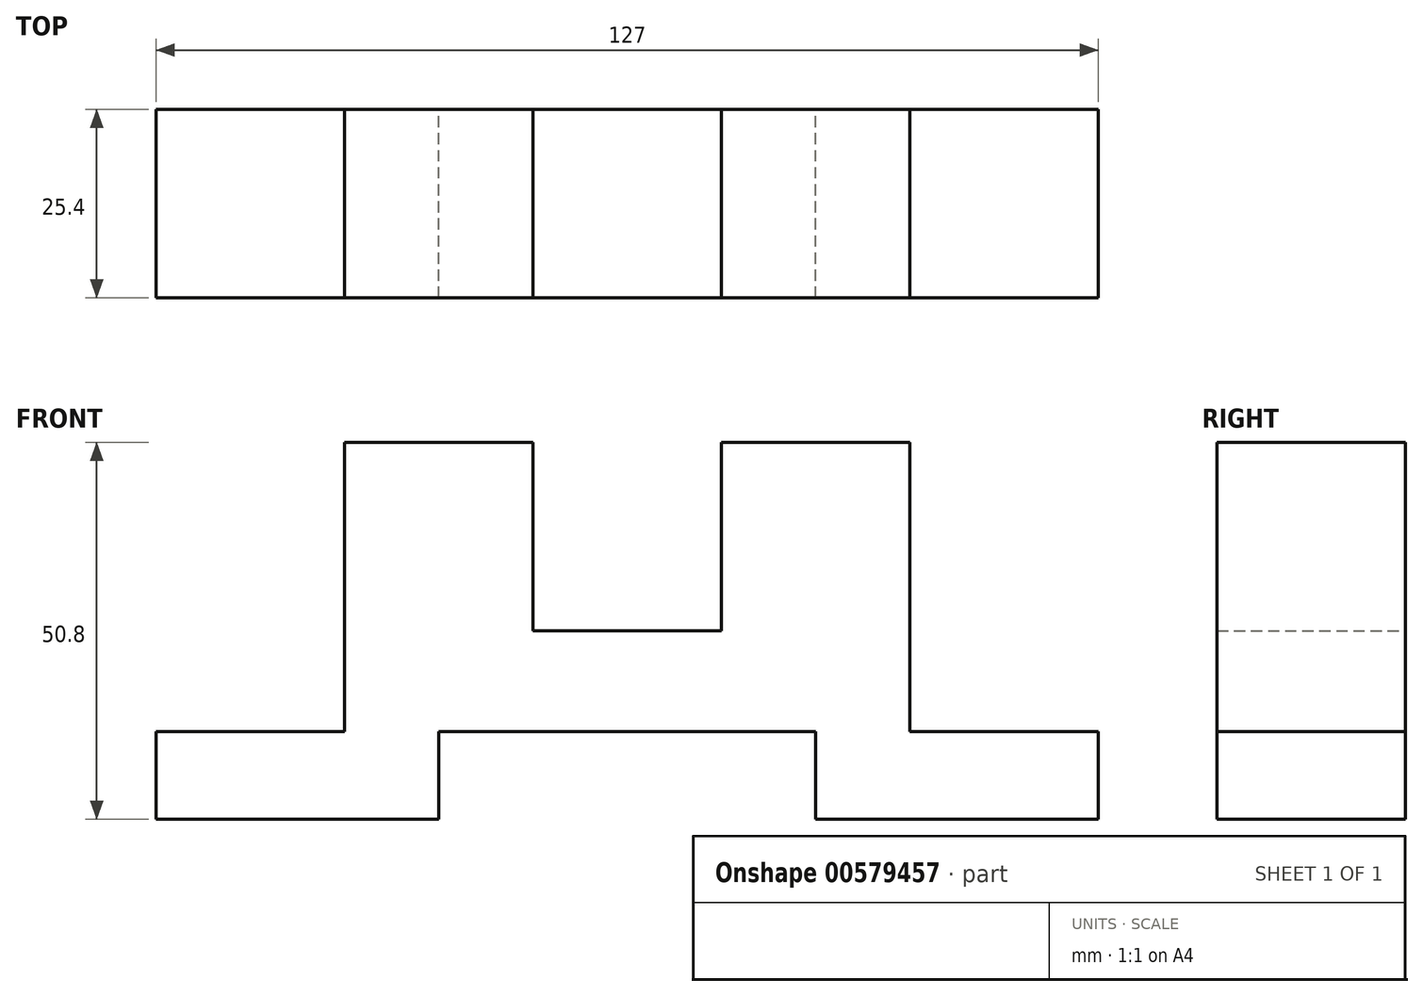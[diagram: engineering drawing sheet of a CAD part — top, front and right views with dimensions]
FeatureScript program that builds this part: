
annotation { "Feature Type Name" : "Feature", "Feature Type Description" : "" }
export const myFeature = defineFeature(function(context is Context, id is Id, definition is map)
    precondition{}
    {
        {
            var Q0;
            Q0=qCreatedBy(makeId("Front.planeOp"),FACE);
            var sketch = newSketch(context, id + "F0", { "sketchPlane" : qUnion([Q0])});
            skLineSegment(sketch, "E0", {"start": v(-17, 0) * mm, "end": v(33.8, 0) * mm});
            skLineSegment(sketch, "E1", {"start": v(33.8, 0) * mm, "end": v(33.8, -11.8) * mm});
            skLineSegment(sketch, "E2", {"start": v(33.8, -11.8) * mm, "end": v(71.9, -11.8) * mm});
            skLineSegment(sketch, "E3", {"start": v(71.9, -11.8) * mm, "end": v(71.9, 0) * mm});
            skLineSegment(sketch, "E4", {"start": v(71.9, 0) * mm, "end": v(46.5, 0) * mm});
            skLineSegment(sketch, "E5", {"start": v(46.5, 0) * mm, "end": v(46.5, 39) * mm});
            skLineSegment(sketch, "E6", {"start": v(46.5, 39) * mm, "end": v(21.1, 39) * mm});
            skLineSegment(sketch, "E7", {"start": v(21.1, 39) * mm, "end": v(21.1, 13.6) * mm});
            skLineSegment(sketch, "E8", {"start": v(21.1, 13.6) * mm, "end": v(-4.3, 13.6) * mm});
            skLineSegment(sketch, "E9", {"start": v(-4.3, 13.6) * mm, "end": v(-4.3, 39) * mm});
            skLineSegment(sketch, "E10", {"start": v(-4.3, 39) * mm, "end": v(-29.7, 39) * mm});
            skLineSegment(sketch, "E11", {"start": v(-29.7, 39) * mm, "end": v(-29.7, 0) * mm});
            skLineSegment(sketch, "E12", {"start": v(-29.7, 0) * mm, "end": v(-55.1, 0) * mm});
            skLineSegment(sketch, "E13", {"start": v(-55.1, 0) * mm, "end": v(-55.1, -11.8) * mm});
            skLineSegment(sketch, "E14", {"start": v(-55.1, -11.8) * mm, "end": v(-17, -11.8) * mm});
            skLineSegment(sketch, "E15", {"start": v(-17, -11.8) * mm, "end": v(-17, 0) * mm});
            skSolve(sketch);
        }
        {
            var Q0;
            Q0=makeQuery(id+"F0.imprint","IMPRINT",FACE,{"disambiguationData":[TD([[makeQuery(id+"F0.imprint","IMPRINT",EDGE,{"derivedFrom":sQuery(id+"F0.wireOp",EDGE,"E0")}),1.0]])]});
            extrude(context, id + "F1", {"entities" : qUnion([Q0]), "depth" : 25.4 * mm, "offsetDistance" : 25.4 * mm});
        }
    });
